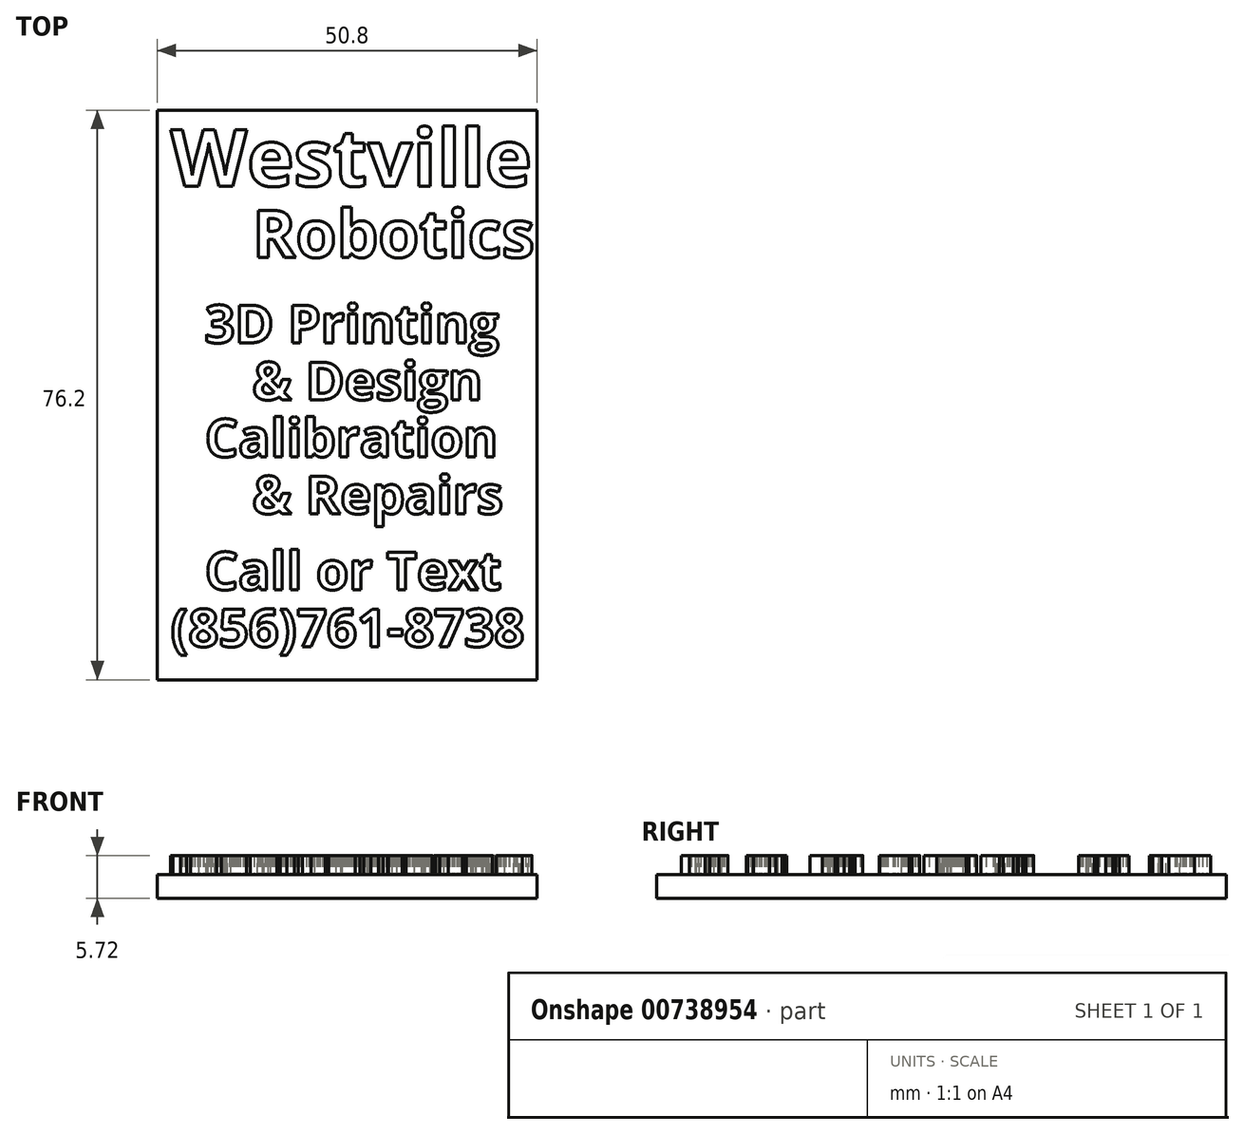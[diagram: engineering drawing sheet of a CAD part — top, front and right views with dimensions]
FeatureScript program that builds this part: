
annotation { "Feature Type Name" : "Feature", "Feature Type Description" : "" }
export const myFeature = defineFeature(function(context is Context, id is Id, definition is map)
    precondition{}
    {
        {
            var Q0;
            Q0=qCreatedBy(makeId("Top.planeOp"),FACE);
            var sketch = newSketch(context, id + "F0", { "sketchPlane" : qUnion([Q0])});
            skLineSegment(sketch, "E0.bottom", {"start": v(25.4, -38.1) * mm, "end": v(-25.4, -38.1) * mm});
            skLineSegment(sketch, "E0.top", {"start": v(25.4, 38.1) * mm, "end": v(-25.4, 38.1) * mm});
            skLineSegment(sketch, "E0.left", {"start": v(25.4, -38.1) * mm, "end": v(25.4, 38.1) * mm});
            skLineSegment(sketch, "E0.right", {"start": v(-25.4, -38.1) * mm, "end": v(-25.4, 38.1) * mm});
            skPoint(sketch, "E0.middle", {"position": v(0, 0) * mm});
            skSolve(sketch);
        }
        {
            var Q0;
            Q0=makeQuery(id+"F0.imprint","IMPRINT",FACE,{"disambiguationData":[TD([[makeQuery(id+"F0.imprint","IMPRINT",EDGE,{"derivedFrom":sQuery(id+"F0.wireOp",EDGE,"E0.bottom")}),-1.0]])]});
            extrude(context, id + "F1", {"entities" : qUnion([Q0]), "depth" : 3.17 * mm, "offsetDistance" : 25.4 * mm});
        }
        {
            var Q0;
            Q0=makeQuery(id+"F1.opExtrude","CAP_FACE",FACE,{"disambiguationData":[OSD([sQuery(id+"F0.wireOp",EDGE,"E0.bottom"),sQuery(id+"F0.wireOp",EDGE,"E0.top"),sQuery(id+"F0.wireOp",EDGE,"E0.left"),sQuery(id+"F0.wireOp",EDGE,"E0.right")])],"isStart":false});
            var sketch = newSketch(context, id + "F2", { "sketchPlane" : qUnion([Q0])});
            skText(sketch, "E1", { "text": "Westville", "fontName": "OpenSans-Bold.ttf"});
            skText(sketch, "E2", { "text": "Robotics", "fontName": "OpenSans-Bold.ttf"});
            skText(sketch, "E3", { "text": "3D Printing", "fontName": "OpenSans-Bold.ttf"});
            skText(sketch, "E4", { "text": "& Design", "fontName": "OpenSans-Bold.ttf"});
            skText(sketch, "E5", { "text": "Calibration", "fontName": "OpenSans-Bold.ttf"});
            skText(sketch, "E6", { "text": "& Repairs", "fontName": "OpenSans-Bold.ttf"});
            skText(sketch, "E7", { "text": "(856)761-8738", "fontName": "OpenSans-Bold.ttf"});
            skText(sketch, "E8", { "text": "Call or Text", "fontName": "OpenSans-Bold.ttf"});
            const initialGuessF2  = {"E1": [-0.02362, 0.02794, 1, 0, 0.00762], "E2": [-0.0127, 0.01841, 1, 0, 0.00635], "E3": [-0.01905, 0.00698, 1, 0, 0.00508], "E4": [-0.0127, -0.00064, 1, 0, 0.00508], "E5": [-0.01905, -0.00826, 1, 0, 0.00508], "E6": [-0.0127, -0.01588, 1, 0, 0.00508], "E7": [-0.02362, -0.03366, 1, 0, 0.00508], "E8": [-0.01905, -0.02604, 1, 0, 0.00508]};
            skSetInitialGuess(sketch, initialGuessF2);
            skSolve(sketch);
        }
        {
            var Q0;
            Q0 = qSketchRegion(id + "F2", true);
            extrude(context, id + "F3", {"entities" : qUnion([Q0]), "operationType" : NewBodyOperationType.ADD, "depth" : 2.54 * mm, "offsetDistance" : 25.4 * mm});
        }
    });
